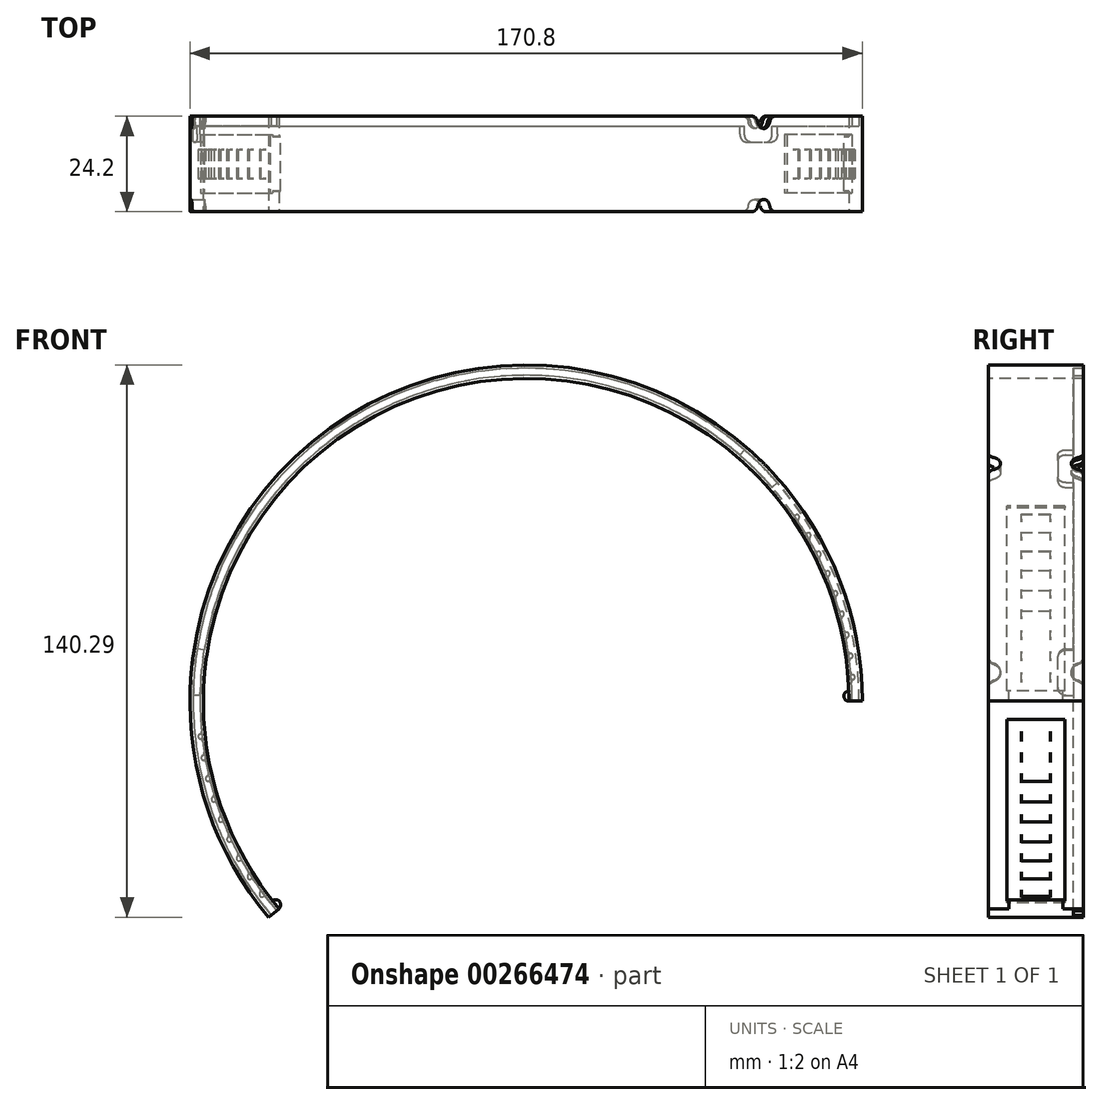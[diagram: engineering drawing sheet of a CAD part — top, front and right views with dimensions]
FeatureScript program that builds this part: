
annotation { "Feature Type Name" : "Feature", "Feature Type Description" : "" }
export const myFeature = defineFeature(function(context is Context, id is Id, definition is map)
    precondition{}
    {
        {
            var Q0;
            Q0=qCreatedBy(makeId("Front.planeOp"),FACE);
            var sketch = newSketch(context, id + "F0", { "sketchPlane" : qUnion([Q0])});
            skArc(sketch, "E0", {"start": v(82, 0) * mm, "mid": v(-28.05, 77.05) * mm, "end": v(-62.82, -52.7) * mm});
            skLineSegment(sketch, "E1", {"start": v(-62.82, -52.7) * mm, "end": v(0, 0) * mm, "construction": true});
            skLineSegment(sketch, "E2", {"start": v(82, 0) * mm, "end": v(0, 0) * mm, "construction": true});
            skSolve(sketch);
        }
        {
            var Q0;
            Q0=qCreatedBy(makeId("Top.planeOp"),FACE);
            var sketch = newSketch(context, id + "F1", { "sketchPlane" : qUnion([Q0])});
            skLineSegment(sketch, "E3.bottom", {"start": v(82, 0) * mm, "end": v(85.4, 0) * mm});
            skLineSegment(sketch, "E3.top", {"start": v(82, -24.2) * mm, "end": v(85.4, -24.2) * mm});
            skLineSegment(sketch, "E3.left", {"start": v(82, 0) * mm, "end": v(82, -24.2) * mm});
            skLineSegment(sketch, "E3.right", {"start": v(85.4, 0) * mm, "end": v(85.4, -24.2) * mm});
            skSolve(sketch);
        }
        {
            var Q0;
            Q0=makeQuery(id+"F1.imprint","IMPRINT",FACE,{"disambiguationData":[TD([[makeQuery(id+"F1.imprint","IMPRINT",EDGE,{"derivedFrom":sQuery(id+"F1.wireOp",EDGE,"E3.bottom")}),-1.0]])]});
            var Q1;
            Q1=sQuery(id+"F0.wireOp",EDGE,"E0");
            sweep(context, id + "F2", {"profiles" : qUnion([Q0]), "path" : qUnion([Q1])});
        }
        {
            var Q0;
            Q0=qCreatedBy(makeId("Top.planeOp"),FACE);
            var sketch = newSketch(context, id + "F3", { "sketchPlane" : qUnion([Q0])});
            skLineSegment(sketch, "E4", {"start": v(0, 0) * mm, "end": v(0, -49.4) * mm});
            skSolve(sketch);
        }
        {
            var Q0;
            Q0=qCreatedBy(makeId("Top.planeOp"),FACE);
            var Q1;
            Q1=sQuery(id+"F3.wireOp",EDGE,"E4");
            cPlane(context, id + "F4", {"entities" : qUnion([Q0, Q1]), "cplaneType" : CPlaneType.LINE_ANGLE, "offset" : 25 * mm, "angle" : 315 * degree, "width" : 150 * mm, "height" : 150 * mm});
        }
        {
            var Q0;
            Q0=makeQuery(id+"F2.opSweep","CAP_FACE",FACE,{"disambiguationData":[OSD([sQuery(id+"F0.wireOp",VERTEX,"E0.end"),sQuery(id+"F1.wireOp",EDGE,"E3.bottom"),sQuery(id+"F1.wireOp",EDGE,"E3.top"),sQuery(id+"F1.wireOp",EDGE,"E3.left"),sQuery(id+"F1.wireOp",EDGE,"E3.right")])],"isStart":false});
            var sketch = newSketch(context, id + "F5", { "sketchPlane" : qUnion([Q0])});
            skLineSegment(sketch, "E5.bottom", {"start": v(-82.8, 0) * mm, "end": v(-84.6, 0) * mm});
            skLineSegment(sketch, "E5.top", {"start": v(-82.8, 2.5) * mm, "end": v(-84.6, 2.5) * mm});
            skLineSegment(sketch, "E5.left", {"start": v(-82.8, 0) * mm, "end": v(-82.8, 2.5) * mm});
            skLineSegment(sketch, "E5.right", {"start": v(-84.6, 0) * mm, "end": v(-84.6, 2.5) * mm});
            skSolve(sketch);
        }
        {
            var Q0;
            Q0=makeQuery(id+"F5.imprint","IMPRINT",FACE,{"disambiguationData":[TD([[makeQuery(id+"F5.imprint","IMPRINT",EDGE,{"derivedFrom":sQuery(id+"F5.wireOp",EDGE,"E5.bottom")}),1.0]])]});
            var Q1;
            Q1=makeQuery(id+"F2.opSweep","SWEPT_EDGE",EDGE,{"disambiguationData":[OSD([sQuery(id+"F0.wireOp",EDGE,"E0"),sQuery(id+"F1.wireOp",EDGE,"E3.bottom"),sQuery(id+"F1.wireOp",EDGE,"E3.left")])]});
            sweep(context, id + "F6", {"operationType" : NewBodyOperationType.REMOVE, "profiles" : qUnion([Q0]), "path" : qUnion([Q1])});
        }
        {
            var Q0;
            Q0=qCreatedBy(id+"F4.planeOp",FACE);
            var sketch = newSketch(context, id + "F7", { "sketchPlane" : qUnion([Q0])});
            skArc(sketch, "E6", {"start": v(1.43, -2.15) * mm, "mid": v(3.1, 0) * mm, "end": v(1.43, 2.15) * mm});
            skArc(sketch, "E7", {"start": v(22.77, 2.15) * mm, "mid": v(21.1, 0) * mm, "end": v(22.77, -2.15) * mm});
            skLineSegment(sketch, "E8", {"start": v(21.1, 0) * mm, "end": v(3.1, 0) * mm, "construction": true});
            skPoint(sketch, "E8.startSnap0", {"position": v(21.1, 0) * mm});
            skPoint(sketch, "E8.endSnap0", {"position": v(3.1, 0) * mm});
            skArc(sketch, "E9", {"start": v(22.77, 2.15) * mm, "mid": v(23.8, 2.83) * mm, "end": v(24.2, 4) * mm});
            skArc(sketch, "E10", {"start": v(22.77, -2.15) * mm, "mid": v(23.8, -2.83) * mm, "end": v(24.2, -4) * mm});
            skArc(sketch, "E11", {"start": v(1.43, 2.15) * mm, "mid": v(0.4, 2.83) * mm, "end": v(0, 4) * mm});
            skArc(sketch, "E12", {"start": v(1.43, -2.15) * mm, "mid": v(0.4, -2.83) * mm, "end": v(0, -4) * mm});
            skLineSegment(sketch, "E13", {"start": v(0, -4) * mm, "end": v(0, 4) * mm});
            skLineSegment(sketch, "E14", {"start": v(24.2, 4) * mm, "end": v(24.2, -4) * mm});
            skLineSegment(sketch, "E15", {"start": v(3.1, 0) * mm, "end": v(0, 0) * mm, "construction": true});
            skLineSegment(sketch, "E16", {"start": v(21.1, 0) * mm, "end": v(24.2, 0) * mm, "construction": true});
            skSolve(sketch);
        }
        {
            var Q0;
            Q0 = qSketchRegion(id + "F7", true);
            extrude(context, id + "F8", {"entities" : qUnion([Q0]), "operationType" : NewBodyOperationType.REMOVE, "endBound" : BoundingType.THROUGH_ALL, "oppositeDirection" : true, "depth" : 25 * mm});
        }
        {
            var Q0;
            Q0=qCreatedBy(makeId("Top.planeOp"),FACE);
            var Q1;
            Q1=sQuery(id+"F3.wireOp",EDGE,"E4");
            cPlane(context, id + "F9", {"entities" : qUnion([Q0, Q1]), "cplaneType" : CPlaneType.LINE_ANGLE, "offset" : 25 * mm, "angle" : 265 * degree, "width" : 150 * mm, "height" : 150 * mm});
        }
        {
            var Q0;
            Q0=qCreatedBy(id+"F9.planeOp",FACE);
            var sketch = newSketch(context, id + "F10", { "sketchPlane" : qUnion([Q0])});
            skLineSegment(sketch, "E17", {"start": v(0, 4) * mm, "end": v(0, -4) * mm});
            skArc(sketch, "E18", {"start": v(1.43, -2.15) * mm, "mid": v(0.4, -2.83) * mm, "end": v(0, -4) * mm});
            skArc(sketch, "E19", {"start": v(0, 4) * mm, "mid": v(0.4, 2.83) * mm, "end": v(1.43, 2.15) * mm});
            skArc(sketch, "E20", {"start": v(1.43, 2.15) * mm, "mid": v(3.1, 0) * mm, "end": v(1.43, -2.15) * mm});
            skLineSegment(sketch, "E21", {"start": v(0, 0) * mm, "end": v(24.2, 0) * mm, "construction": true});
            skLineSegment(sketch, "E22", {"start": v(12.1, 0) * mm, "end": v(12.1, 14.2) * mm, "construction": true});
            skArc(sketch, "E23.MirrorCS", {"start": v(24.2, 4) * mm, "mid": v(23.8, 2.83) * mm, "end": v(22.77, 2.15) * mm});
            skLineSegment(sketch, "E24.MirrorCS", {"start": v(24.2, 4) * mm, "end": v(24.2, -4) * mm});
            skArc(sketch, "E25.MirrorCS", {"start": v(22.77, 2.15) * mm, "mid": v(21.1, 0) * mm, "end": v(22.77, -2.15) * mm});
            skArc(sketch, "E26.MirrorCS", {"start": v(22.77, -2.15) * mm, "mid": v(23.8, -2.83) * mm, "end": v(24.2, -4) * mm});
            skSolve(sketch);
        }
        {
            var Q0;
            Q0 = qSketchRegion(id + "F10", true);
            extrude(context, id + "F11", {"entities" : qUnion([Q0]), "operationType" : NewBodyOperationType.REMOVE, "endBound" : BoundingType.THROUGH_ALL, "depth" : 25 * mm});
        }
        {
            var Q0;
            {var subQ0=sQuery(id+"F1.wireOp",EDGE,"E3.left");var subQ1=sQuery(id+"F1.wireOp",EDGE,"E3.bottom");var subQ2=makeQuery(id+"F2.opSweep","CAP_FACE",FACE,{"disambiguationData":[OSD([sQuery(id+"F0.wireOp",VERTEX,"E0.end"),subQ1,sQuery(id+"F1.wireOp",EDGE,"E3.top"),subQ0,sQuery(id+"F1.wireOp",EDGE,"E3.right")])],"isStart":false});var subQ3=sQuery(id+"F0.wireOp",EDGE,"E0");Q0=makeQuery(id+"F11.boolean.opBoolean","SPLIT",FACE,{"disambiguationData":[TD([subQ2])],"derivedFrom":makeQuery(id+"F8.boolean.opBoolean","SPLIT",FACE,{"disambiguationData":[TD([subQ2])],"derivedFrom":makeQuery(id+"F6.boolean.opBoolean","COPY",FACE,{"derivedFrom":makeQuery(id+"F6.opSweep","SWEPT_FACE",FACE,{"disambiguationData":[OSD([subQ3,subQ1,subQ0,sQuery(id+"F5.wireOp",EDGE,"E5.top")])]})})})});}
            var sketch = newSketch(context, id + "F12", { "sketchPlane" : qUnion([Q0])});
            skArc(sketch, "E27", {"start": v(84.59, 1.48) * mm, "mid": v(84.28, 7.37) * mm, "end": v(83.56, 13.23) * mm});
            skArc(sketch, "E28", {"start": v(82.79, 1.45) * mm, "mid": v(82.48, 7.22) * mm, "end": v(81.78, 12.95) * mm});
            skLineSegment(sketch, "E29", {"start": v(82.79, 1.45) * mm, "end": v(84.59, 1.48) * mm});
            skLineSegment(sketch, "E30", {"start": v(81.78, 12.95) * mm, "end": v(83.56, 13.23) * mm});
            skArc(sketch, "E31", {"start": v(-55.5, 63.85) * mm, "mid": v(-59.82, 59.82) * mm, "end": v(-63.85, 55.5) * mm});
            skArc(sketch, "E32", {"start": v(-54.32, 62.49) * mm, "mid": v(-58.55, 58.55) * mm, "end": v(-62.49, 54.32) * mm});
            skLineSegment(sketch, "E33", {"start": v(-62.49, 54.32) * mm, "end": v(-63.85, 55.5) * mm});
            skLineSegment(sketch, "E34", {"start": v(-54.32, 62.49) * mm, "end": v(-55.5, 63.85) * mm});
            skSolve(sketch);
        }
        {
            var Q0;
            Q0 = qSketchRegion(id + "F12", true);
            extrude(context, id + "F13", {"entities" : qUnion([Q0]), "operationType" : NewBodyOperationType.REMOVE, "oppositeDirection" : true, "depth" : 4 * mm});
        }
        {
            var Q0;
            Q0=makeQuery(id+"F13.boolean.opBoolean","COPY",EDGE,{"derivedFrom":makeQuery(id+"F13.opExtrude","CAP_EDGE",EDGE,{"disambiguationData":[OSD([sQuery(id+"F12.wireOp",EDGE,"E34")])],"isStart":false})});
            var Q1;
            Q1=makeQuery(id+"F13.boolean.opBoolean","COPY",EDGE,{"derivedFrom":makeQuery(id+"F13.opExtrude","CAP_EDGE",EDGE,{"disambiguationData":[OSD([sQuery(id+"F12.wireOp",EDGE,"E33")])],"isStart":false})});
            var Q2;
            Q2=makeQuery(id+"F13.boolean.opBoolean","COPY",EDGE,{"derivedFrom":makeQuery(id+"F13.opExtrude","CAP_EDGE",EDGE,{"disambiguationData":[OSD([sQuery(id+"F12.wireOp",EDGE,"E33")])],"isStart":true})});
            var Q3;
            Q3=makeQuery(id+"F13.boolean.opBoolean","COPY",EDGE,{"derivedFrom":makeQuery(id+"F13.opExtrude","CAP_EDGE",EDGE,{"disambiguationData":[OSD([sQuery(id+"F12.wireOp",EDGE,"E34")])],"isStart":true})});
            var Q4;
            Q4=makeQuery(id+"F13.boolean.opBoolean","COPY",EDGE,{"derivedFrom":makeQuery(id+"F13.opExtrude","CAP_EDGE",EDGE,{"disambiguationData":[OSD([sQuery(id+"F12.wireOp",EDGE,"E30")])],"isStart":false})});
            var Q5;
            Q5=makeQuery(id+"F13.boolean.opBoolean","COPY",EDGE,{"derivedFrom":makeQuery(id+"F13.opExtrude","CAP_EDGE",EDGE,{"disambiguationData":[OSD([sQuery(id+"F12.wireOp",EDGE,"E30")])],"isStart":true})});
            var Q6;
            Q6=makeQuery(id+"F13.boolean.opBoolean","COPY",EDGE,{"derivedFrom":makeQuery(id+"F13.opExtrude","CAP_EDGE",EDGE,{"disambiguationData":[OSD([sQuery(id+"F12.wireOp",EDGE,"E29")])],"isStart":false})});
            var Q7;
            Q7=makeQuery(id+"F13.boolean.opBoolean","COPY",EDGE,{"derivedFrom":makeQuery(id+"F13.opExtrude","CAP_EDGE",EDGE,{"disambiguationData":[OSD([sQuery(id+"F12.wireOp",EDGE,"E29")])],"isStart":true})});
            fillet(context, id + "F14", {"entities" : qUnion([Q0, Q1, Q2, Q3, Q4, Q5, Q6, Q7]), "radius" : 2 * mm, "tangentPropagation" : true, "allowEdgeOverflow" : false});
        }
        {
            var Q0;
            {var subQ2=sQuery(id+"F1.wireOp",EDGE,"E3.top");var subQ4=sQuery(id+"F0.wireOp",EDGE,"E0");Q0=makeQuery(id+"F11.boolean.opBoolean","SPLIT",FACE,{"disambiguationData":[TD([makeQuery(id+"F11.opExtrude","SWEPT_FACE",FACE,{"disambiguationData":[OSD([sQuery(id+"F10.wireOp",EDGE,"E26.MirrorCS")])]})])],"derivedFrom":makeQuery(id+"F8.boolean.opBoolean","SPLIT",FACE,{"disambiguationData":[TD([makeQuery(id+"F8.opExtrude","SWEPT_FACE",FACE,{"disambiguationData":[OSD([sQuery(id+"F7.wireOp",EDGE,"E9")])]})])],"derivedFrom":makeQuery(id+"F2.opSweep","SWEPT_FACE",FACE,{"disambiguationData":[OSD([subQ4,subQ2])]})})});}
            var Q1;
            {var subQ1=sQuery(id+"F1.wireOp",EDGE,"E3.left");var subQ3=sQuery(id+"F1.wireOp",EDGE,"E3.bottom");var subQ5=sQuery(id+"F0.wireOp",EDGE,"E0");var subQ6=makeQuery(id+"F2.opSweep","SWEPT_FACE",FACE,{"disambiguationData":[OSD([subQ5,subQ1])]});Q1=makeQuery(id+"F11.boolean.opBoolean","SPLIT",FACE,{"disambiguationData":[TD([makeQuery(id+"F11.opExtrude","SWEPT_FACE",FACE,{"disambiguationData":[OSD([sQuery(id+"F10.wireOp",EDGE,"E18")])]})])],"derivedFrom":makeQuery(id+"F8.boolean.opBoolean","SPLIT",FACE,{"disambiguationData":[TD([makeQuery(id+"F8.opExtrude","SWEPT_FACE",FACE,{"disambiguationData":[OSD([sQuery(id+"F7.wireOp",EDGE,"E11")])]})])],"derivedFrom":makeQuery(id+"F6.boolean.opBoolean","SPLIT",FACE,{"disambiguationData":[TD([subQ6])],"derivedFrom":makeQuery(id+"F2.opSweep","SWEPT_FACE",FACE,{"disambiguationData":[OSD([subQ5,subQ3])]})})})});}
            cPlane(context, id + "F15", {"entities" : qUnion([Q0, Q1]), "cplaneType" : CPlaneType.MID_PLANE, "offset" : 25 * mm, "width" : 150 * mm, "height" : 150 * mm});
        }
        {
            var Q0;
            Q0=qCreatedBy(id+"F15.planeOp",FACE);
            var sketch = newSketch(context, id + "F16", { "sketchPlane" : qUnion([Q0])});
            skArc(sketch, "E35", {"start": v(-65.07, -51.2) * mm, "mid": v(-77.45, -29.27) * mm, "end": v(-82.67, -4.62) * mm});
            skLineSegment(sketch, "E36", {"start": v(-65.07, -51.2) * mm, "end": v(0, 0) * mm});
            skLineSegment(sketch, "E37", {"start": v(-82.67, -4.62) * mm, "end": v(0, 0) * mm});
            skLineSegment(sketch, "E38", {"start": v(0, 0) * mm, "end": v(82.76, 2.6) * mm});
            skLineSegment(sketch, "E39", {"start": v(66.3, 49.6) * mm, "end": v(0, 0) * mm});
            skArc(sketch, "E40", {"start": v(82.76, 2.6) * mm, "mid": v(78.15, 27.37) * mm, "end": v(66.3, 49.6) * mm});
            skSolve(sketch);
        }
        {
            var Q0;
            Q0 = qSketchRegion(id + "F16", true);
            extrude(context, id + "F17", {"entities" : qUnion([Q0]), "operationType" : NewBodyOperationType.REMOVE, "endBound" : BoundingType.SYMMETRIC, "oppositeDirection" : true, "depth" : 14.8 * mm});
        }
        {
            var Q0;
            Q0=qCreatedBy(id+"F15.planeOp",FACE);
            var sketch = newSketch(context, id + "F18", { "sketchPlane" : qUnion([Q0])});
            skArc(sketch, "E41", {"start": v(-62.82, -52.7) * mm, "mid": v(-62.64, -50.9) * mm, "end": v(-64.44, -50.71) * mm});
            skLineSegment(sketch, "E42", {"start": v(-64.44, -50.71) * mm, "end": v(-65.26, -51.35) * mm});
            skLineSegment(sketch, "E43", {"start": v(-65.26, -51.35) * mm, "end": v(-63.58, -53.35) * mm});
            skLineSegment(sketch, "E44", {"start": v(-63.58, -53.35) * mm, "end": v(-62.82, -52.7) * mm});
            skLineSegment(sketch, "E45.0", {"start": v(82, 0) * mm, "end": v(82.76, 0) * mm});
            skLineSegment(sketch, "E45.1", {"start": v(81.96, 2.57) * mm, "end": v(82.76, 2.6) * mm});
            skArc(sketch, "E46", {"start": v(81.96, 2.57) * mm, "mid": v(80.71, 1.27) * mm, "end": v(82, 0) * mm});
            skLineSegment(sketch, "E47", {"start": v(82.76, 2.6) * mm, "end": v(82.76, 0) * mm});
            skPoint(sketch, "E48.orphan", {"position": v(85.4, 0) * mm});
            skSolve(sketch);
        }
        {
            var Q0;
            Q0 = qSketchRegion(id + "F18", true);
            extrude(context, id + "F19", {"entities" : qUnion([Q0]), "operationType" : NewBodyOperationType.ADD, "endBound" : BoundingType.SYMMETRIC, "depth" : 13.8 * mm});
        }
        {
            var Q0;
            Q0=qCreatedBy(id+"F15.planeOp",FACE);
            var sketch = newSketch(context, id + "F20", { "sketchPlane" : qUnion([Q0])});
            skArc(sketch, "E49.0.0", {"start": v(-67.55, -47.89) * mm, "mid": v(-66.82, -48.9) * mm, "end": v(-66.07, -49.9) * mm});
            skArc(sketch, "E49.0.2", {"start": v(-65.07, -51.2) * mm, "mid": v(-77.45, -29.27) * mm, "end": v(-82.67, -4.62) * mm});
            skArc(sketch, "E50", {"start": v(-67.59, -48.69) * mm, "mid": v(-67.62, -49.5) * mm, "end": v(-66.84, -49.7) * mm});
            skArc(sketch, "E51", {"start": v(-66.07, -49.9) * mm, "mid": v(-66.42, -49.67) * mm, "end": v(-66.84, -49.7) * mm});
            skArc(sketch, "E52", {"start": v(-67.59, -48.69) * mm, "mid": v(-67.43, -48.3) * mm, "end": v(-67.55, -47.89) * mm});
            skPoint(sketch, "E53.orphan", {"position": v(-82.67, -4.62) * mm});
            skPoint(sketch, "E54.orphan", {"position": v(-65.07, -51.2) * mm});
            skLineSegment(sketch, "E55", {"start": v(-67.62, -49.5) * mm, "end": v(-66.82, -48.9) * mm, "construction": true});
            skArc(sketch, "E56.1.0", {"start": v(-70.63, -44.16) * mm, "mid": v(-70.44, -43.78) * mm, "end": v(-70.53, -43.37) * mm});
            skArc(sketch, "E56.1.1", {"start": v(-69.2, -45.48) * mm, "mid": v(-69.53, -45.22) * mm, "end": v(-69.95, -45.23) * mm});
            skArc(sketch, "E56.1.2", {"start": v(-70.63, -44.16) * mm, "mid": v(-70.72, -44.96) * mm, "end": v(-69.95, -45.23) * mm});
            skArc(sketch, "E56.1.3", {"start": v(-70.53, -43.37) * mm, "mid": v(-69.87, -44.43) * mm, "end": v(-69.2, -45.48) * mm});
            skLineSegment(sketch, "E56.1.4", {"start": v(-70.72, -44.96) * mm, "end": v(-69.87, -44.43) * mm, "construction": true});
            skArc(sketch, "E56.2.0", {"start": v(-73.36, -39.45) * mm, "mid": v(-73.16, -39.08) * mm, "end": v(-73.22, -38.66) * mm});
            skArc(sketch, "E56.2.1", {"start": v(-72.02, -40.86) * mm, "mid": v(-72.34, -40.58) * mm, "end": v(-72.76, -40.55) * mm});
            skArc(sketch, "E56.2.2", {"start": v(-73.36, -39.45) * mm, "mid": v(-73.5, -40.24) * mm, "end": v(-72.76, -40.55) * mm});
            skArc(sketch, "E56.2.3", {"start": v(-73.22, -38.66) * mm, "mid": v(-72.63, -39.76) * mm, "end": v(-72.02, -40.86) * mm});
            skLineSegment(sketch, "E56.2.4", {"start": v(-73.5, -40.24) * mm, "end": v(-72.63, -39.76) * mm, "construction": true});
            skArc(sketch, "E56.3.0", {"start": v(-75.79, -34.57) * mm, "mid": v(-75.55, -34.21) * mm, "end": v(-75.6, -33.8) * mm});
            skArc(sketch, "E56.3.1", {"start": v(-74.54, -36.06) * mm, "mid": v(-74.84, -35.76) * mm, "end": v(-75.26, -35.7) * mm});
            skArc(sketch, "E56.3.2", {"start": v(-75.79, -34.57) * mm, "mid": v(-75.98, -35.35) * mm, "end": v(-75.26, -35.7) * mm});
            skArc(sketch, "E56.3.3", {"start": v(-75.6, -33.8) * mm, "mid": v(-75.07, -34.93) * mm, "end": v(-74.54, -36.06) * mm});
            skLineSegment(sketch, "E56.3.4", {"start": v(-75.98, -35.35) * mm, "end": v(-75.07, -34.93) * mm, "construction": true});
            skArc(sketch, "E56.4.0", {"start": v(-77.89, -29.54) * mm, "mid": v(-77.63, -29.2) * mm, "end": v(-77.64, -28.77) * mm});
            skArc(sketch, "E56.4.1", {"start": v(-76.74, -31.1) * mm, "mid": v(-77.01, -30.79) * mm, "end": v(-77.43, -30.7) * mm});
            skArc(sketch, "E56.4.2", {"start": v(-77.89, -29.54) * mm, "mid": v(-78.13, -30.3) * mm, "end": v(-77.43, -30.7) * mm});
            skArc(sketch, "E56.4.3", {"start": v(-77.64, -28.77) * mm, "mid": v(-77.2, -29.94) * mm, "end": v(-76.74, -31.1) * mm});
            skLineSegment(sketch, "E56.4.4", {"start": v(-78.13, -30.3) * mm, "end": v(-77.2, -29.94) * mm, "construction": true});
            skArc(sketch, "E56.5.0", {"start": v(-79.65, -24.38) * mm, "mid": v(-79.37, -24.06) * mm, "end": v(-79.36, -23.63) * mm});
            skArc(sketch, "E56.5.1", {"start": v(-78.6, -26.02) * mm, "mid": v(-78.86, -25.68) * mm, "end": v(-79.27, -25.58) * mm});
            skArc(sketch, "E56.5.2", {"start": v(-79.65, -24.38) * mm, "mid": v(-79.94, -25.13) * mm, "end": v(-79.27, -25.58) * mm});
            skArc(sketch, "E56.5.3", {"start": v(-79.36, -23.63) * mm, "mid": v(-78.99, -24.83) * mm, "end": v(-78.6, -26.02) * mm});
            skLineSegment(sketch, "E56.5.4", {"start": v(-79.94, -25.13) * mm, "end": v(-78.99, -24.83) * mm, "construction": true});
            skArc(sketch, "E56.6.0", {"start": v(-81.07, -19.12) * mm, "mid": v(-80.78, -18.81) * mm, "end": v(-80.73, -18.4) * mm});
            skArc(sketch, "E56.6.1", {"start": v(-80.14, -20.82) * mm, "mid": v(-80.37, -20.47) * mm, "end": v(-80.78, -20.34) * mm});
            skArc(sketch, "E56.6.2", {"start": v(-81.07, -19.12) * mm, "mid": v(-81.42, -19.85) * mm, "end": v(-80.78, -20.34) * mm});
            skArc(sketch, "E56.6.3", {"start": v(-80.73, -18.4) * mm, "mid": v(-80.44, -19.61) * mm, "end": v(-80.14, -20.82) * mm});
            skLineSegment(sketch, "E56.6.4", {"start": v(-81.42, -19.85) * mm, "end": v(-80.44, -19.61) * mm, "construction": true});
            skArc(sketch, "E56.7.0", {"start": v(-82.15, -13.77) * mm, "mid": v(-81.84, -13.5) * mm, "end": v(-81.76, -13.07) * mm});
            skArc(sketch, "E56.7.1", {"start": v(-81.33, -15.54) * mm, "mid": v(-81.54, -15.17) * mm, "end": v(-81.93, -15.01) * mm});
            skArc(sketch, "E56.7.2", {"start": v(-82.15, -13.77) * mm, "mid": v(-82.54, -14.48) * mm, "end": v(-81.93, -15.01) * mm});
            skArc(sketch, "E56.7.3", {"start": v(-81.76, -13.07) * mm, "mid": v(-81.55, -14.3) * mm, "end": v(-81.33, -15.54) * mm});
            skLineSegment(sketch, "E56.7.4", {"start": v(-82.54, -14.48) * mm, "end": v(-81.55, -14.3) * mm, "construction": true});
            skArc(sketch, "E56.8.0", {"start": v(-82.88, -8.37) * mm, "mid": v(-82.54, -8.11) * mm, "end": v(-82.44, -7.7) * mm});
            skArc(sketch, "E56.8.1", {"start": v(-82.17, -10.18) * mm, "mid": v(-82.36, -9.8) * mm, "end": v(-82.74, -9.62) * mm});
            skArc(sketch, "E56.8.2", {"start": v(-82.88, -8.37) * mm, "mid": v(-83.3, -9.05) * mm, "end": v(-82.74, -9.62) * mm});
            skArc(sketch, "E56.8.3", {"start": v(-82.44, -7.7) * mm, "mid": v(-82.32, -8.94) * mm, "end": v(-82.17, -10.18) * mm});
            skLineSegment(sketch, "E56.8.4", {"start": v(-83.3, -9.05) * mm, "end": v(-82.32, -8.94) * mm, "construction": true});
            skLineSegment(sketch, "E56.anchor1", {"start": v(0, 0) * mm, "end": v(-68.07, -48.26) * mm, "construction": true});
            skLineSegment(sketch, "E56.anchor2", {"start": v(0, 0) * mm, "end": v(-83.08, -7.76) * mm, "construction": true});
            skArc(sketch, "E57.1.0", {"start": v(82.48, 7.31) * mm, "mid": v(82.65, 6.92) * mm, "end": v(83.03, 6.73) * mm});
            skArc(sketch, "E57.1.1", {"start": v(80.45, 21.58) * mm, "mid": v(80.17, 21.27) * mm, "end": v(80.13, 20.85) * mm});
            skLineSegment(sketch, "E57.1.2", {"start": v(83.57, 6.14) * mm, "end": v(82.58, 6.06) * mm, "construction": true});
            skArc(sketch, "E57.1.3", {"start": v(80.13, 20.85) * mm, "mid": v(79.8, 22.06) * mm, "end": v(79.47, 23.26) * mm});
            skArc(sketch, "E57.1.4", {"start": v(82.17, 10.21) * mm, "mid": v(82, 11.45) * mm, "end": v(81.82, 12.69) * mm});
            skArc(sketch, "E57.1.5", {"start": v(78.87, 26.8) * mm, "mid": v(79.14, 27.56) * mm, "end": v(78.45, 27.99) * mm});
            skArc(sketch, "E57.1.6", {"start": v(83.12, 5.47) * mm, "mid": v(83.57, 6.14) * mm, "end": v(83.03, 6.73) * mm});
            skArc(sketch, "E57.1.7", {"start": v(79.47, 23.26) * mm, "mid": v(79.71, 22.92) * mm, "end": v(80.12, 22.8) * mm});
            skArc(sketch, "E57.1.8", {"start": v(81.82, 12.69) * mm, "mid": v(82.02, 12.32) * mm, "end": v(82.4, 12.15) * mm});
            skLineSegment(sketch, "E57.1.9", {"start": v(80.77, 22.32) * mm, "end": v(79.8, 22.06) * mm, "construction": true});
            skArc(sketch, "E57.1.10", {"start": v(78.87, 26.8) * mm, "mid": v(78.6, 26.47) * mm, "end": v(78.6, 26.05) * mm});
            skArc(sketch, "E57.1.11", {"start": v(75.75, 33.43) * mm, "mid": v(76.04, 33.12) * mm, "end": v(76.46, 33.06) * mm});
            skArc(sketch, "E57.1.12", {"start": v(82.66, 4.82) * mm, "mid": v(82.58, 6.06) * mm, "end": v(82.48, 7.31) * mm});
            skArc(sketch, "E57.1.13", {"start": v(80.45, 21.58) * mm, "mid": v(80.77, 22.32) * mm, "end": v(80.12, 22.8) * mm});
            skArc(sketch, "E57.1.14", {"start": v(74.7, 36.86) * mm, "mid": v(74.86, 37.65) * mm, "end": v(74.13, 37.99) * mm});
            skArc(sketch, "E57.1.15", {"start": v(74.52, 36.08) * mm, "mid": v(73.97, 37.2) * mm, "end": v(73.4, 38.32) * mm});
            skLineSegment(sketch, "E57.1.16", {"start": v(74.86, 37.65) * mm, "end": v(73.97, 37.2) * mm, "construction": true});
            skLineSegment(sketch, "E57.1.17", {"start": v(83, 11.6) * mm, "end": v(82, 11.45) * mm, "construction": true});
            skArc(sketch, "E57.1.18", {"start": v(78.6, 26.05) * mm, "mid": v(78.2, 27.23) * mm, "end": v(77.77, 28.4) * mm});
            skArc(sketch, "E57.1.19", {"start": v(82.58, 10.9) * mm, "mid": v(83, 11.6) * mm, "end": v(82.4, 12.15) * mm});
            skArc(sketch, "E57.1.20", {"start": v(77.77, 28.4) * mm, "mid": v(78.04, 28.08) * mm, "end": v(78.45, 27.99) * mm});
            skArc(sketch, "E57.1.21", {"start": v(72.13, 41.67) * mm, "mid": v(71.93, 41.3) * mm, "end": v(72, 40.88) * mm});
            skArc(sketch, "E57.1.22", {"start": v(70.74, 43.04) * mm, "mid": v(71.06, 42.77) * mm, "end": v(71.49, 42.76) * mm});
            skArc(sketch, "E57.1.23", {"start": v(72.13, 41.67) * mm, "mid": v(72.24, 42.47) * mm, "end": v(71.49, 42.76) * mm});
            skArc(sketch, "E57.1.24", {"start": v(72, 40.88) * mm, "mid": v(71.38, 41.96) * mm, "end": v(70.74, 43.04) * mm});
            skLineSegment(sketch, "E57.1.25", {"start": v(72.24, 42.47) * mm, "end": v(71.38, 41.96) * mm, "construction": true});
            skArc(sketch, "E57.1.26", {"start": v(74.7, 36.86) * mm, "mid": v(74.47, 36.5) * mm, "end": v(74.52, 36.08) * mm});
            skArc(sketch, "E57.1.27", {"start": v(73.4, 38.32) * mm, "mid": v(73.7, 38.03) * mm, "end": v(74.13, 37.99) * mm});
            skArc(sketch, "E57.1.28", {"start": v(83.12, 5.47) * mm, "mid": v(82.77, 5.22) * mm, "end": v(82.66, 4.82) * mm});
            skLineSegment(sketch, "E57.1.29", {"start": v(79.14, 27.56) * mm, "end": v(78.2, 27.23) * mm, "construction": true});
            skLineSegment(sketch, "E57.1.30", {"start": v(82.06, 17) * mm, "end": v(81.08, 16.8) * mm, "construction": true});
            skArc(sketch, "E57.1.31", {"start": v(76.72, 31.13) * mm, "mid": v(76.25, 32.29) * mm, "end": v(75.75, 33.43) * mm});
            skArc(sketch, "E57.1.32", {"start": v(82.58, 10.9) * mm, "mid": v(82.26, 10.63) * mm, "end": v(82.17, 10.21) * mm});
            skArc(sketch, "E57.1.33", {"start": v(80.82, 18.01) * mm, "mid": v(81.04, 17.65) * mm, "end": v(81.44, 17.5) * mm});
            skArc(sketch, "E57.1.34", {"start": v(81.7, 16.28) * mm, "mid": v(82.06, 17) * mm, "end": v(81.44, 17.5) * mm});
            skArc(sketch, "E57.1.35", {"start": v(81.7, 16.28) * mm, "mid": v(81.38, 15.98) * mm, "end": v(81.32, 15.57) * mm});
            skArc(sketch, "E57.1.36", {"start": v(81.32, 15.57) * mm, "mid": v(81.08, 16.8) * mm, "end": v(80.82, 18.01) * mm});
            skLineSegment(sketch, "E57.1.37", {"start": v(77.17, 32.68) * mm, "end": v(76.25, 32.29) * mm, "construction": true});
            skArc(sketch, "E57.1.38", {"start": v(76.95, 31.9) * mm, "mid": v(76.7, 31.55) * mm, "end": v(76.72, 31.13) * mm});
            skArc(sketch, "E57.1.39", {"start": v(76.95, 31.9) * mm, "mid": v(77.17, 32.68) * mm, "end": v(76.46, 33.06) * mm});
            skArc(sketch, "E57.1.40", {"start": v(69.18, 45.5) * mm, "mid": v(68.48, 46.54) * mm, "end": v(67.77, 47.57) * mm});
            skArc(sketch, "E57.1.41", {"start": v(69.25, 46.3) * mm, "mid": v(69.3, 47.1) * mm, "end": v(68.54, 47.34) * mm});
            skArc(sketch, "E57.1.42", {"start": v(67.77, 47.57) * mm, "mid": v(68.11, 47.32) * mm, "end": v(68.54, 47.34) * mm});
            skArc(sketch, "E57.1.43", {"start": v(69.25, 46.3) * mm, "mid": v(69.07, 45.91) * mm, "end": v(69.18, 45.5) * mm});
            skLineSegment(sketch, "E57.1.44", {"start": v(69.3, 47.1) * mm, "end": v(68.48, 46.54) * mm, "construction": true});
            skLineSegment(sketch, "E57.anchor1", {"start": v(0, 0) * mm, "end": v(-67.62, -49.5) * mm, "construction": true});
            skLineSegment(sketch, "E57.anchor2", {"start": v(0, 0) * mm, "end": v(69.3, 47.1) * mm, "construction": true});
            skSolve(sketch);
        }
        {
            var Q0;
            Q0 = qSketchRegion(id + "F20", true);
            extrude(context, id + "F21", {"entities" : qUnion([Q0]), "operationType" : NewBodyOperationType.REMOVE, "endBound" : BoundingType.SYMMETRIC, "oppositeDirection" : true, "depth" : 7.4 * mm});
        }
    });
